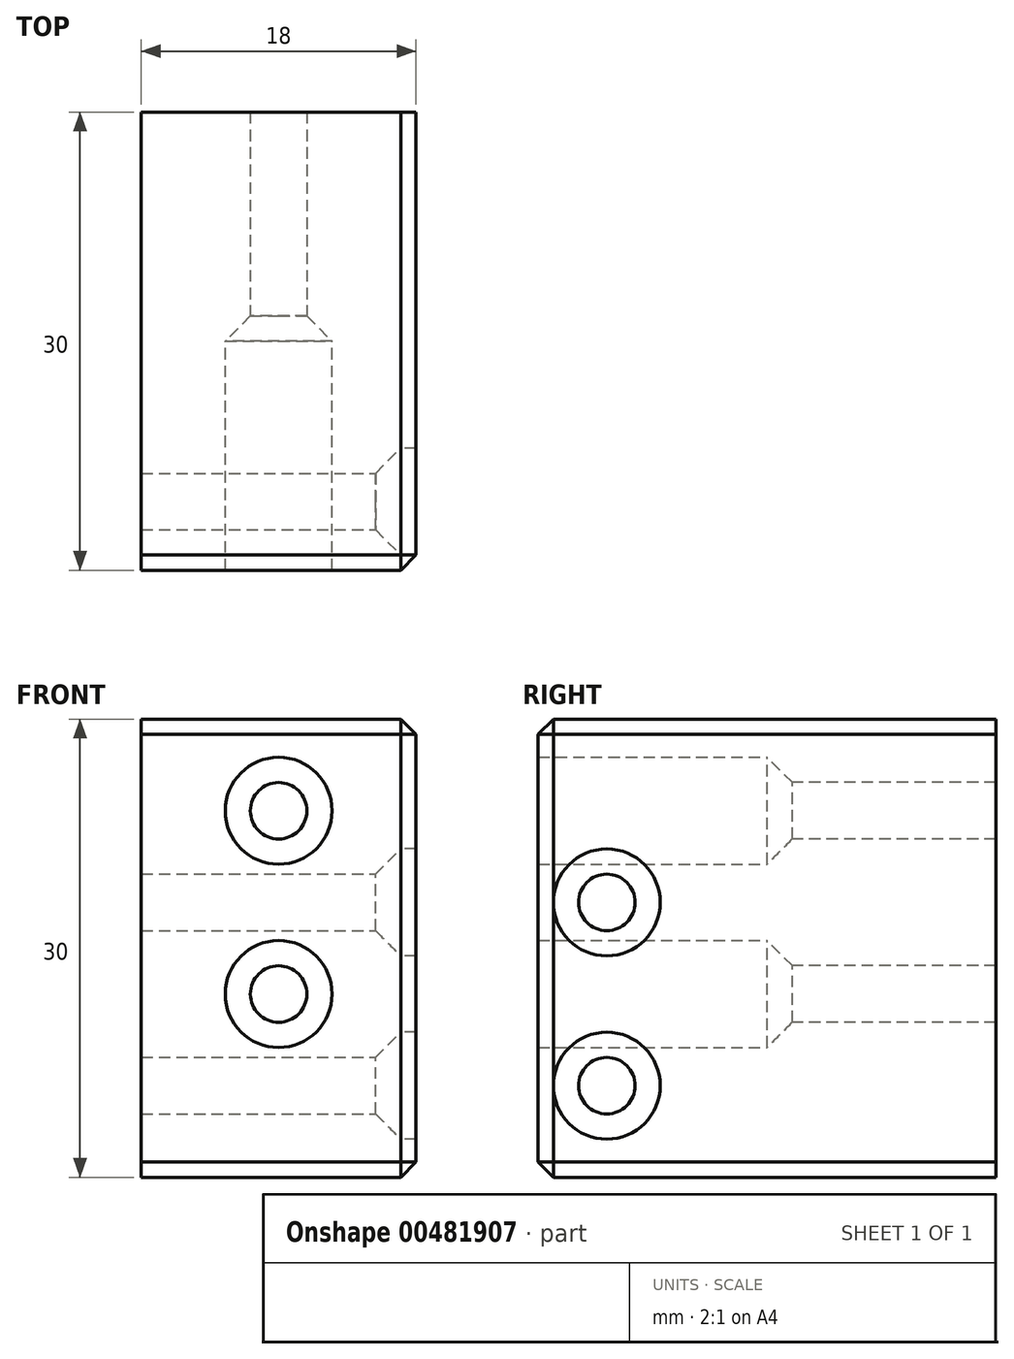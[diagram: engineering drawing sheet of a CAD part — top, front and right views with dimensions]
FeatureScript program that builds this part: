
annotation { "Feature Type Name" : "Feature", "Feature Type Description" : "" }
export const myFeature = defineFeature(function(context is Context, id is Id, definition is map)
    precondition{}
    {
        {
            var Q0;
            Q0=qCreatedBy(makeId("Front.planeOp"),FACE);
            var sketch = newSketch(context, id + "F0", { "sketchPlane" : qUnion([Q0])});
            skLineSegment(sketch, "E0.bottom", {"start": v(-9, 0) * mm, "end": v(9, 0) * mm});
            skLineSegment(sketch, "E0.top", {"start": v(-9, 30) * mm, "end": v(9, 30) * mm});
            skLineSegment(sketch, "E0.left", {"start": v(-9, 0) * mm, "end": v(-9, 30) * mm});
            skLineSegment(sketch, "E0.right", {"start": v(9, 0) * mm, "end": v(9, 30) * mm});
            skSolve(sketch);
        }
        {
            var Q0;
            Q0=makeQuery(id+"F0.imprint","IMPRINT",FACE,{"disambiguationData":[TD([[makeQuery(id+"F0.imprint","IMPRINT",EDGE,{"derivedFrom":sQuery(id+"F0.wireOp",EDGE,"E0.bottom")}),1.0]])]});
            extrude(context, id + "F1", {"entities" : qUnion([Q0]), "depth" : 30 * mm});
        }
        {
            var Q0;
            Q0=makeQuery(id+"F1.opExtrude","CAP_FACE",FACE,{"disambiguationData":[OSD([sQuery(id+"F0.wireOp",EDGE,"E0.bottom"),sQuery(id+"F0.wireOp",EDGE,"E0.top"),sQuery(id+"F0.wireOp",EDGE,"E0.left"),sQuery(id+"F0.wireOp",EDGE,"E0.right")])],"isStart":false});
            cPlane(context, id + "F2", {"entities" : qUnion([Q0]), "cplaneType" : CPlaneType.OFFSET, "offset" : 15 * mm, "oppositeDirection" : true, "width" : 150 * mm, "height" : 150 * mm});
        }
        {
            var Q0;
            Q0=qCreatedBy(id+"F2.planeOp",FACE);
            var sketch = newSketch(context, id + "F3", { "sketchPlane" : qUnion([Q0])});
            skPoint(sketch, "E1", {"position": v(0, 24) * mm});
            skPoint(sketch, "E2", {"position": v(0, 12) * mm});
            skSolve(sketch);
        }
        {
            var Q0;
            Q0=sQuery(id+"F3.wireOp",VERTEX,"E1");
            var Q1;
            Q1=sQuery(id+"F3.wireOp",VERTEX,"E2");
            var Q2;
            Q2=makeQuery(id+"F1.opExtrude","SWEPT_BODY",BODY,{"disambiguationData":[OSD([sQuery(id+"F0.wireOp",EDGE,"E0.bottom"),sQuery(id+"F0.wireOp",EDGE,"E0.top"),sQuery(id+"F0.wireOp",EDGE,"E0.left"),sQuery(id+"F0.wireOp",EDGE,"E0.right")])]});
            hole(context, id + "F4", {"style" : HoleStyle.SIMPLE, "endStyle" : HoleEndStyle.THROUGH, "oppositeDirection" : true, "holeDiameter" : 7 * mm, "isTappedThrough" : true, "tappedDepth" : 12 * mm, "tapClearance" : 3, "locations" : qUnion([Q0, Q1]), "scope" : qUnion([Q2])});
        }
        {
            var Q0;
            Q0=sQuery(id+"F3.wireOp",VERTEX,"E1");
            var Q1;
            Q1=sQuery(id+"F3.wireOp",VERTEX,"E2");
            var Q2;
            Q2=makeQuery(id+"F1.opExtrude","SWEPT_BODY",BODY,{"disambiguationData":[OSD([sQuery(id+"F0.wireOp",EDGE,"E0.bottom"),sQuery(id+"F0.wireOp",EDGE,"E0.top"),sQuery(id+"F0.wireOp",EDGE,"E0.left"),sQuery(id+"F0.wireOp",EDGE,"E0.right")])]});
            hole(context, id + "F5", {"style" : HoleStyle.C_SINK, "endStyle" : HoleEndStyle.THROUGH, "holeDiameter" : 3.7 * mm, "cSinkDiameter" : 7 * mm, "cSinkAngle" : 90 * degree, "isTappedThrough" : true, "tappedDepth" : 12 * mm, "tapClearance" : 3, "locations" : qUnion([Q0, Q1]), "scope" : qUnion([Q2])});
        }
        {
            var Q0;
            Q0=makeQuery(id+"F1.opExtrude","SWEPT_FACE",FACE,{"disambiguationData":[OSD([sQuery(id+"F0.wireOp",EDGE,"E0.right")])]});
            cPlane(context, id + "F6", {"entities" : qUnion([Q0]), "cplaneType" : CPlaneType.OFFSET, "offset" : 1 * mm, "oppositeDirection" : true, "width" : 150 * mm, "height" : 150 * mm});
        }
        {
            var Q0;
            Q0=qCreatedBy(id+"F6.planeOp",FACE);
            var sketch = newSketch(context, id + "F7", { "sketchPlane" : qUnion([Q0])});
            skPoint(sketch, "E3", {"position": v(-25.5, 18) * mm});
            skPoint(sketch, "E4", {"position": v(-25.5, 6) * mm});
            skSolve(sketch);
        }
        {
            var Q0;
            Q0=sQuery(id+"F7.wireOp",VERTEX,"E3");
            var Q1;
            Q1=sQuery(id+"F7.wireOp",VERTEX,"E4");
            var Q2;
            Q2=makeQuery(id+"F1.opExtrude","SWEPT_BODY",BODY,{"disambiguationData":[OSD([sQuery(id+"F0.wireOp",EDGE,"E0.bottom"),sQuery(id+"F0.wireOp",EDGE,"E0.top"),sQuery(id+"F0.wireOp",EDGE,"E0.left"),sQuery(id+"F0.wireOp",EDGE,"E0.right")])]});
            hole(context, id + "F8", {"style" : HoleStyle.SIMPLE, "endStyle" : HoleEndStyle.THROUGH, "oppositeDirection" : true, "holeDiameter" : 7 * mm, "isTappedThrough" : true, "tappedDepth" : 12 * mm, "tapClearance" : 3, "locations" : qUnion([Q0, Q1]), "scope" : qUnion([Q2])});
        }
        {
            var Q0;
            Q0=sQuery(id+"F7.wireOp",VERTEX,"E3");
            var Q1;
            Q1=sQuery(id+"F7.wireOp",VERTEX,"E4");
            var Q2;
            Q2=makeQuery(id+"F1.opExtrude","SWEPT_BODY",BODY,{"disambiguationData":[OSD([sQuery(id+"F0.wireOp",EDGE,"E0.bottom"),sQuery(id+"F0.wireOp",EDGE,"E0.top"),sQuery(id+"F0.wireOp",EDGE,"E0.left"),sQuery(id+"F0.wireOp",EDGE,"E0.right")])]});
            hole(context, id + "F9", {"style" : HoleStyle.C_SINK, "endStyle" : HoleEndStyle.THROUGH, "holeDiameter" : 3.7 * mm, "cSinkDiameter" : 7 * mm, "cSinkAngle" : 90 * degree, "isTappedThrough" : true, "tappedDepth" : 12 * mm, "tapClearance" : 3, "locations" : qUnion([Q0, Q1]), "scope" : qUnion([Q2])});
        }
        {
            var Q0;
            Q0=makeQuery(id+"F1.opExtrude","CAP_EDGE",EDGE,{"disambiguationData":[OSD([sQuery(id+"F0.wireOp",EDGE,"E0.right")])],"isStart":false});
            var Q1;
            Q1=makeQuery(id+"F1.opExtrude","SWEPT_EDGE",EDGE,{"disambiguationData":[OSD([sQuery(id+"F0.wireOp",EDGE,"E0.top"),sQuery(id+"F0.wireOp",EDGE,"E0.right")])]});
            var Q2;
            Q2=makeQuery(id+"F1.opExtrude","CAP_EDGE",EDGE,{"disambiguationData":[OSD([sQuery(id+"F0.wireOp",EDGE,"E0.top")])],"isStart":false});
            var Q3;
            Q3=makeQuery(id+"F1.opExtrude","SWEPT_EDGE",EDGE,{"disambiguationData":[OSD([sQuery(id+"F0.wireOp",EDGE,"E0.bottom"),sQuery(id+"F0.wireOp",EDGE,"E0.right")])]});
            var Q4;
            Q4=makeQuery(id+"F1.opExtrude","CAP_EDGE",EDGE,{"disambiguationData":[OSD([sQuery(id+"F0.wireOp",EDGE,"E0.bottom")])],"isStart":false});
            chamfer(context, id + "F10", {"entities" : qUnion([Q0, Q1, Q2, Q3, Q4]), "width" : 1 * mm, "tangentPropagation" : true});
        }
    });
